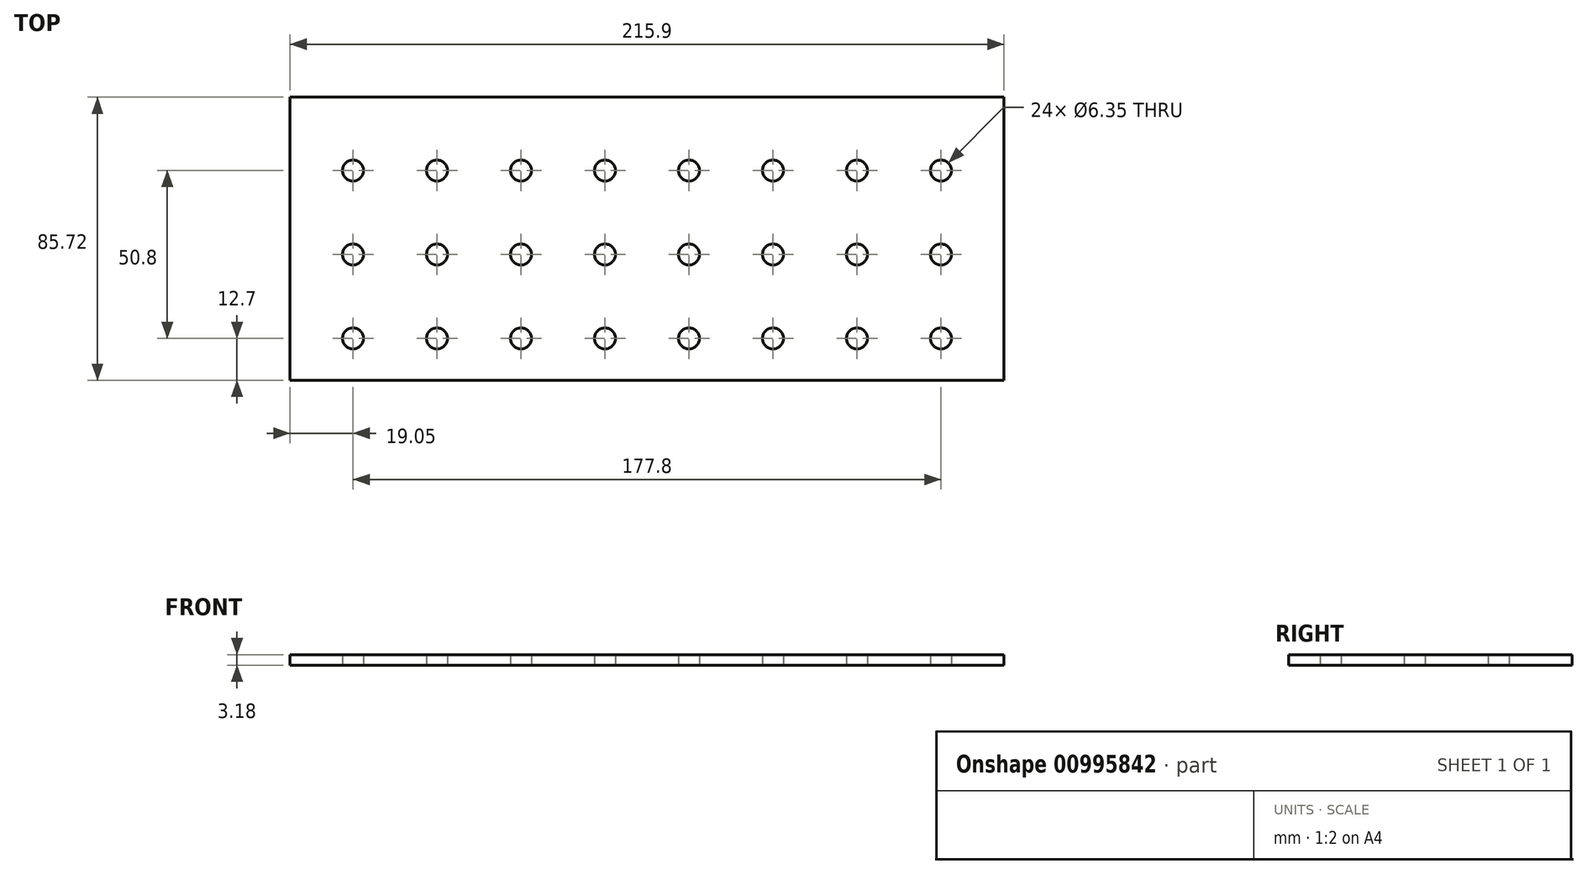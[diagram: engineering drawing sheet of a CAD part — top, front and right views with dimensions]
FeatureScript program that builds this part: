
annotation { "Feature Type Name" : "Feature", "Feature Type Description" : "" }
export const myFeature = defineFeature(function(context is Context, id is Id, definition is map)
    precondition{}
    {
        {
            var Q0;
            Q0=qCreatedBy(makeId("Top.planeOp"),FACE);
            var sketch = newSketch(context, id + "F0", { "sketchPlane" : qUnion([Q0])});
            skLineSegment(sketch, "E0.bottom", {"start": v(0, 0) * mm, "end": v(215.9, 0) * mm});
            skLineSegment(sketch, "E0.top", {"start": v(0, 85.73) * mm, "end": v(215.9, 85.73) * mm});
            skLineSegment(sketch, "E0.left", {"start": v(0, 0) * mm, "end": v(0, 85.73) * mm});
            skLineSegment(sketch, "E0.right", {"start": v(215.9, 0) * mm, "end": v(215.9, 85.73) * mm});
            skLineSegment(sketch, "E1", {"start": v(0, 0) * mm, "end": v(19.05, 0) * mm});
            skCircle(sketch, "E2", {"center": v(19.05, 12.7) * mm, "radius": 3.18 * mm});
            skCircle(sketch, "E3.1.0.0", {"center": v(44.45, 12.7) * mm, "radius": 3.18 * mm});
            skCircle(sketch, "E3.2.0.0", {"center": v(69.85, 12.7) * mm, "radius": 3.18 * mm});
            skCircle(sketch, "E3.3.0.0", {"center": v(95.25, 12.7) * mm, "radius": 3.18 * mm});
            skCircle(sketch, "E3.4.0.0", {"center": v(120.65, 12.7) * mm, "radius": 3.18 * mm});
            skCircle(sketch, "E3.5.0.0", {"center": v(146.05, 12.7) * mm, "radius": 3.18 * mm});
            skCircle(sketch, "E3.6.0.0", {"center": v(171.45, 12.7) * mm, "radius": 3.18 * mm});
            skCircle(sketch, "E3.7.0.0", {"center": v(196.85, 12.7) * mm, "radius": 3.18 * mm});
            skCircle(sketch, "E4.0.1.0", {"center": v(196.85, 38.1) * mm, "radius": 3.18 * mm});
            skCircle(sketch, "E4.0.1.1", {"center": v(146.05, 38.1) * mm, "radius": 3.18 * mm});
            skCircle(sketch, "E4.0.1.2", {"center": v(95.25, 38.1) * mm, "radius": 3.18 * mm});
            skCircle(sketch, "E4.0.1.3", {"center": v(44.45, 38.1) * mm, "radius": 3.18 * mm});
            skCircle(sketch, "E4.0.1.4", {"center": v(120.65, 38.1) * mm, "radius": 3.18 * mm});
            skCircle(sketch, "E4.0.1.5", {"center": v(19.05, 38.1) * mm, "radius": 3.18 * mm});
            skCircle(sketch, "E4.0.1.6", {"center": v(171.45, 38.1) * mm, "radius": 3.18 * mm});
            skCircle(sketch, "E4.0.1.7", {"center": v(69.85, 38.1) * mm, "radius": 3.18 * mm});
            skCircle(sketch, "E4.0.2.0", {"center": v(196.85, 63.5) * mm, "radius": 3.18 * mm});
            skCircle(sketch, "E4.0.2.1", {"center": v(146.05, 63.5) * mm, "radius": 3.18 * mm});
            skCircle(sketch, "E4.0.2.2", {"center": v(95.25, 63.5) * mm, "radius": 3.18 * mm});
            skCircle(sketch, "E4.0.2.3", {"center": v(44.45, 63.5) * mm, "radius": 3.18 * mm});
            skCircle(sketch, "E4.0.2.4", {"center": v(120.65, 63.5) * mm, "radius": 3.18 * mm});
            skCircle(sketch, "E4.0.2.5", {"center": v(19.05, 63.5) * mm, "radius": 3.18 * mm});
            skCircle(sketch, "E4.0.2.6", {"center": v(171.45, 63.5) * mm, "radius": 3.18 * mm});
            skCircle(sketch, "E4.0.2.7", {"center": v(69.85, 63.5) * mm, "radius": 3.18 * mm});
            skSolve(sketch);
        }
        {
            var Q0;
            Q0=makeQuery(id+"F0.imprint","IMPRINT",FACE,{"disambiguationData":[TD([[makeQuery(id+"F0.imprint","IMPRINT",EDGE,{"derivedFrom":sQuery(id+"F0.wireOp",EDGE,"E0.bottom")}),1.0]])]});
            extrude(context, id + "F1", {"entities" : qUnion([Q0]), "depth" : 3.17 * mm, "offsetDistance" : 25.4 * mm});
        }
    });
